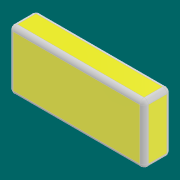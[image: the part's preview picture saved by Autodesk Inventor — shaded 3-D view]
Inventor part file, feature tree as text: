
AUTODESK INVENTOR PART (.ipt)
format: ipt  version: 2020 (Build 240168000, 168)  size: 105,472 bytes
history: native  units: mm
features: extrude x1, fillet x1, sketch x1
ambient origin geometry x8: Origin, YZ Plane, XZ Plane, XY Plane, X Axis, Y Axis, Z Axis, Center Point
bodies: Solid1 (feature_tree)
feature tree (3):
  extrude  "Extrusion1"  Depth=42.0mm
  fillet  "Fillet1"  Radius=19.0mm
  sketch  "Sketch1"  dims[d0=95.0mm d1=42.0mm d2=19.0mm d3=0.0mm d4=3.0mm]
